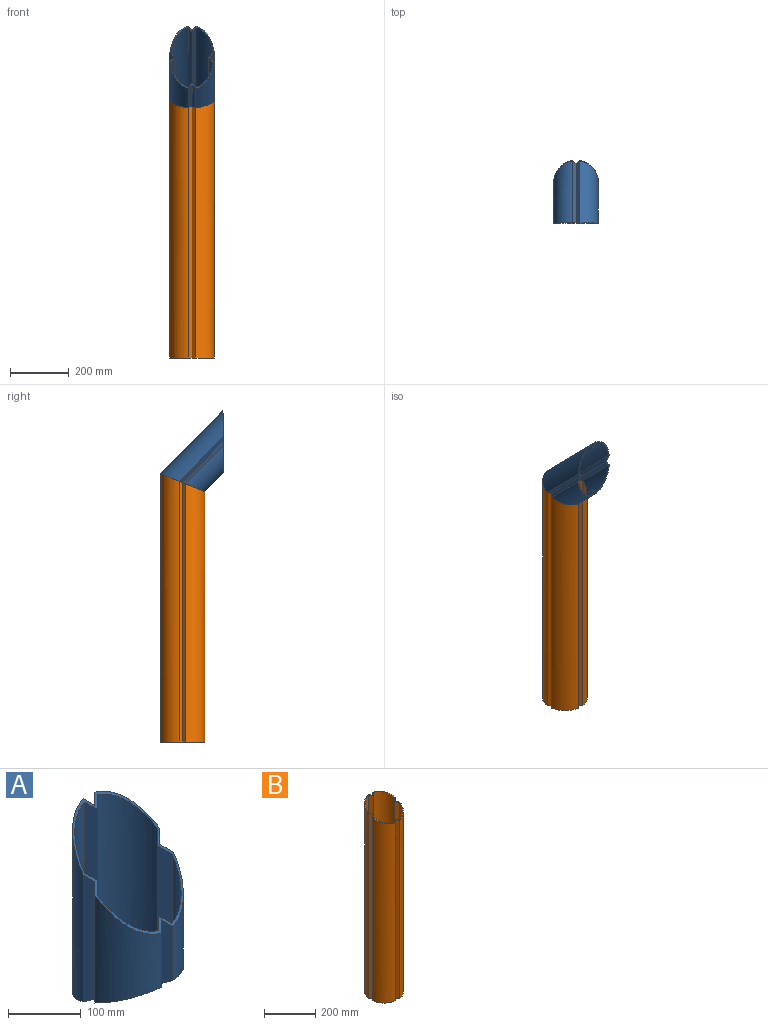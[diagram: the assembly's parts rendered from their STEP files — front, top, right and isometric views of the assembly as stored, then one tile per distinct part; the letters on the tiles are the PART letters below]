
ASSEMBLY  parts=2 mates=1
PART A: 26 faces, bbox 150.4x150.7x303.6 mm
  f0: plane 197.43x13.41mm, normal (0.71,0.71,0), area 3564.1mm2, adj f1,f11,f12,f13
  f1: cylinder r=76.2mm len=178.53mm, axis (0,0,-1), area 11896.9mm2, adj f0,f2,f12,f13
  f2: plane 107.04x11.23mm, normal (-0.71,-0.71,0), area 1573.7mm2, adj f1,f3,f12,f13
  f3: plane 107.04x11.23mm, normal (0.71,-0.71,0), area 1573.7mm2, adj f2,f4,f12,f13
  f4: cylinder r=76.2mm len=181.61mm, axis (0,0,-1), area 12294.9mm2, adj f3,f5,f12,f13
  f5: plane 197.43x11.23mm, normal (-0.71,0.71,0), area 3008.6mm2, adj f4,f6,f12,f13
  f6: plane 213.24x11.23mm, normal (-0.71,-0.71,0), area 3259.7mm2, adj f5,f7,f12,f13
  f7: cylinder r=76.2mm len=303.63mm, axis (0,0,-1), area 26069.6mm2, adj f6,f8,f12,f13
  f8: plane 303.63x11.23mm, normal (0.71,0.71,0), area 4694.5mm2, adj f7,f9,f12,f13
  f9: plane 303.63x11.23mm, normal (-0.71,0.71,0), area 4694.5mm2, adj f8,f10,f12,f13
  f10: cylinder r=76.2mm len=303.63mm, axis (0,0,-1), area 25594.9mm2, adj f9,f11,f12,f13
  f11: plane 216.32x13.41mm, normal (0.71,-0.71,0), area 3922.3mm2, adj f0,f10,f12,f13
  f12: plane 150.74x150.38mm, normal (0,-0.38,-0.93), area 1746.6mm2, adj f0,f1,f2,f3,f4,f5,f6,f7
  f13: plane 150.74x150.74mm, normal (0,-0.71,0.71), area 2286.2mm2, adj f0,f1,f2,f3,f4,f5,f6,f7
  f14: cylinder r=73.03mm len=298.85mm, axis (0,0,-1), area 23424.1mm2, adj f12,f13,f15,f25
  f15: plane 217.81x14.46mm, normal (-0.71,0.71,0), area 4246.8mm2, adj f12,f13,f14,f16
  f16: plane 197.43x14.46mm, normal (-0.71,-0.71,0), area 3829.9mm2, adj f12,f13,f15,f17
  f17: cylinder r=73.03mm len=177.04mm, axis (0,0,-1), area 11229.6mm2, adj f12,f13,f16,f18
  f18: plane 113.37x12.32mm, normal (0.71,0.71,0), area 1824.6mm2, adj f12,f13,f17,f19
  f19: plane 113.37x12.32mm, normal (-0.71,0.71,0), area 1824.6mm2, adj f12,f13,f18,f20
  f20: cylinder r=73.03mm len=180.06mm, axis (0,0,-1), area 11618.2mm2, adj f12,f13,f19,f21
  f21: plane 197.43x12.32mm, normal (0.71,-0.71,0), area 3289.6mm2, adj f12,f13,f20,f22
  f22: plane 214.79x12.32mm, normal (0.71,0.71,0), area 3592.3mm2, adj f12,f13,f21,f23
  f23: cylinder r=73.03mm len=298.85mm, axis (0,0,-1), area 23894.9mm2, adj f12,f13,f22,f24
  f24: plane 298.85x12.32mm, normal (-0.71,-0.71,0), area 5057.4mm2, adj f12,f13,f23,f25
  f25: plane 298.85x12.32mm, normal (0.71,-0.71,0), area 5057.4mm2, adj f12,f13,f14,f24
PART B: 26 faces, bbox 150.4x150.7x914.1 mm
  f0: plane 888.71x13.41mm, normal (0.71,-0.71,0), area 16797.9mm2, adj f1,f23,f24,f25
  f1: cylinder r=76.2mm len=914.06mm, axis (0,0,-1), area 85852.1mm2, adj f0,f2,f24,f25
  f2: plane 914.06x11.23mm, normal (-0.71,0.71,0), area 14474.2mm2, adj f1,f3,f24,f25
  f3: plane 914.06x11.23mm, normal (0.71,0.71,0), area 14474.2mm2, adj f2,f4,f24,f25
  f4: cylinder r=76.2mm len=914.06mm, axis (0,0,-1), area 87815.6mm2, adj f3,f5,f24,f25
  f5: plane 887.82x11.23mm, normal (-0.71,-0.71,0), area 14057.7mm2, adj f4,f6,f24,f25
  f6: plane 883.23x11.23mm, normal (-0.71,0.71,0), area 13984.8mm2, adj f5,f7,f24,f25
  f7: cylinder r=76.2mm len=878.63mm, axis (0,0,-1), area 83816.4mm2, adj f6,f8,f24,f25
  f8: plane 856.98x11.23mm, normal (0.71,-0.71,0), area 13568.2mm2, adj f7,f9,f24,f25
  f9: plane 856.98x11.23mm, normal (-0.71,-0.71,0), area 13568.2mm2, adj f8,f10,f24,f25
  f10: cylinder r=76.2mm len=877.74mm, axis (0,0,-1), area 81875.1mm2, adj f9,f23,f24,f25
  f11: cylinder r=73.03mm len=912.67mm, axis (0,0,-1), area 79285.5mm2, adj f12,f22,f24,f25
  f12: plane 889.14x14.46mm, normal (-0.71,0.71,0), area 18126.8mm2, adj f11,f13,f24,f25
  f13: plane 883.23x14.46mm, normal (-0.71,-0.71,0), area 18005.7mm2, adj f12,f14,f24,f25
  f14: cylinder r=73.03mm len=877.31mm, axis (0,0,-1), area 75745mm2, adj f13,f15,f24,f25
  f15: plane 858.82x12.32mm, normal (0.71,0.71,0), area 14924.6mm2, adj f14,f16,f24,f25
  f16: plane 858.82x12.32mm, normal (-0.71,0.71,0), area 14924.6mm2, adj f15,f17,f24,f25
  f17: cylinder r=73.03mm len=878.18mm, axis (0,0,-1), area 77655.4mm2, adj f16,f18,f24,f25
  f18: plane 883.23x12.32mm, normal (0.71,-0.71,0), area 15350mm2, adj f17,f19,f24,f25
  f19: plane 888.27x12.32mm, normal (0.71,0.71,0), area 15437.9mm2, adj f18,f20,f24,f25
  f20: cylinder r=73.03mm len=912.67mm, axis (0,0,-1), area 81219.7mm2, adj f19,f21,f24,f25
  f21: plane 912.67x12.32mm, normal (-0.71,-0.71,0), area 15863.2mm2, adj f20,f22,f24,f25
  f22: plane 912.67x12.32mm, normal (0.71,-0.71,0), area 15863.2mm2, adj f11,f21,f24,f25
  f23: plane 883.23x13.41mm, normal (0.71,0.71,0), area 16693.9mm2, adj f0,f10,f24,f25
  f24: plane 150.74x150.38mm, normal (0,0,-1), area 1616.6mm2, adj f0,f1,f2,f3,f4,f5,f6,f7
  f25: plane 150.74x150.38mm, normal (0,-0.38,0.93), area 1746.6mm2, adj f0,f1,f2,f3,f4,f5,f6,f7
PLACE A rot(axis=(1,0,0),44.5deg) t=(-159.95,207.68,821.38)mm
PLACE B t=(-159.95,185.83,-39.61)mm
MATE fastened A.f12 <-> B.f25  axis (0,0.38,-0.93) through (-159.95,185.83,843.61)mm
